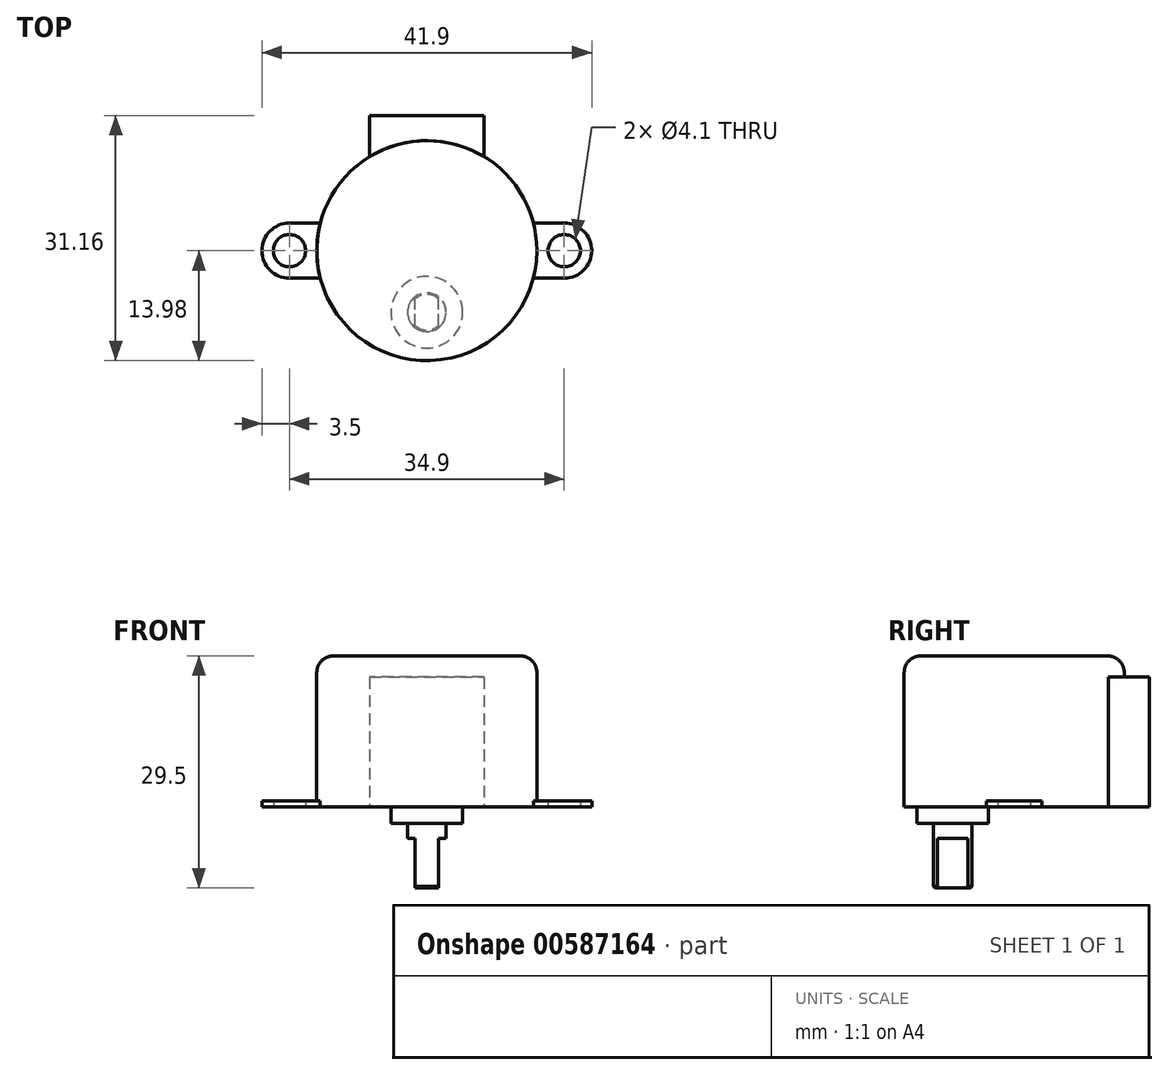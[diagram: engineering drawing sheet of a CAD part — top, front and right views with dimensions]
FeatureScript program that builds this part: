
annotation { "Feature Type Name" : "Feature", "Feature Type Description" : "" }
export const myFeature = defineFeature(function(context is Context, id is Id, definition is map)
    precondition{}
    {
        {
            var Q0;
            Q0=qCreatedBy(makeId("Top.planeOp"),FACE);
            var sketch = newSketch(context, id + "F0", { "sketchPlane" : qUnion([Q0])});
            skArc(sketch, "E0", {"start": v(13.53, 3.5) * mm, "mid": v(0, 13.97) * mm, "end": v(-13.53, 3.5) * mm});
            skLineSegment(sketch, "E1", {"start": v(0, 41.3) * mm, "end": v(0, -21.58) * mm, "construction": true});
            skLineSegment(sketch, "E2", {"start": v(0, 0) * mm, "end": v(20.95, 0) * mm, "construction": true});
            skLineSegment(sketch, "E3.0", {"start": v(13.53, -3.5) * mm, "end": v(17.45, -3.5) * mm});
            skLineSegment(sketch, "E4.0", {"start": v(13.53, 3.5) * mm, "end": v(17.45, 3.5) * mm});
            skCircle(sketch, "E5", {"center": v(17.45, 0) * mm, "radius": 2.05 * mm});
            skArc(sketch, "E6", {"start": v(17.45, -3.5) * mm, "mid": v(20.95, 0) * mm, "end": v(17.45, 3.5) * mm});
            skLineSegment(sketch, "E7.MirrorCS", {"start": v(-13.53, -3.5) * mm, "end": v(-17.45, -3.5) * mm});
            skLineSegment(sketch, "E8.MirrorCS", {"start": v(-13.53, 3.5) * mm, "end": v(-17.45, 3.5) * mm});
            skCircle(sketch, "E9.MirrorC", {"center": v(-17.45, 0) * mm, "radius": 2.05 * mm});
            skArc(sketch, "E10.MirrorCS", {"start": v(-17.45, -3.5) * mm, "mid": v(-20.95, 0) * mm, "end": v(-17.45, 3.5) * mm});
            skArc(sketch, "E11.trimOffspring", {"start": v(-13.53, -3.5) * mm, "mid": v(0, -13.97) * mm, "end": v(13.53, -3.5) * mm});
            skArc(sketch, "E12", {"start": v(-13.53, 3.5) * mm, "mid": v(-13.98, 0) * mm, "end": v(-13.53, -3.5) * mm});
            skArc(sketch, "E13.trimOffspring", {"start": v(13.53, -3.5) * mm, "mid": v(13.98, 0) * mm, "end": v(13.53, 3.5) * mm});
            skSolve(sketch);
        }
        {
            var Q0;
            Q0=makeQuery(id+"F0.imprint","IMPRINT",FACE,{"disambiguationData":[TD([[makeQuery(id+"F0.imprint","IMPRINT",EDGE,{"derivedFrom":sQuery(id+"F0.wireOp",EDGE,"E7.MirrorCS")}),-1.0]])]});
            var Q1;
            Q1=makeQuery(id+"F0.imprint","IMPRINT",FACE,{"disambiguationData":[TD([[makeQuery(id+"F0.imprint","IMPRINT",EDGE,{"derivedFrom":sQuery(id+"F0.wireOp",EDGE,"E3.0")}),1.0]])]});
            extrude(context, id + "F1", {"entities" : qUnion([Q0, Q1]), "depth" : 0.8 * mm});
        }
        {
            var Q0;
            Q0=makeQuery(id+"F0.imprint","IMPRINT",FACE,{"disambiguationData":[TD([[makeQuery(id+"F0.imprint","IMPRINT",EDGE,{"derivedFrom":sQuery(id+"F0.wireOp",EDGE,"E0")}),1.0]])]});
            extrude(context, id + "F2", {"entities" : qUnion([Q0]), "operationType" : NewBodyOperationType.ADD, "depth" : 19.2 * mm});
        }
        {
            var Q0;
            Q0=qCreatedBy(makeId("Top.planeOp"),FACE);
            var sketch = newSketch(context, id + "F3", { "sketchPlane" : qUnion([Q0])});
            skCircle(sketch, "E14", {"center": v(0, -7.82) * mm, "radius": 4.55 * mm});
            skCircle(sketch, "E15", {"center": v(0, -7.82) * mm, "radius": 2.45 * mm});
            skPoint(sketch, "E16", {"position": v(0, -3.27) * mm});
            skLineSegment(sketch, "E17.left", {"start": v(1.47, -9.78) * mm, "end": v(1.47, -5.87) * mm});
            skLineSegment(sketch, "E17.right", {"start": v(-1.48, -9.78) * mm, "end": v(-1.48, -5.87) * mm});
            skLineSegment(sketch, "E18", {"start": v(-1.48, -9.78) * mm, "end": v(1.47, -9.78) * mm, "construction": true});
            skLineSegment(sketch, "E19", {"start": v(-1.48, -5.87) * mm, "end": v(1.47, -5.87) * mm, "construction": true});
            skSolve(sketch);
        }
        {
            var Q0;
            Q0=makeQuery(id+"F3.imprint","IMPRINT",FACE,{"disambiguationData":[TD([[makeQuery(id+"F3.imprint","IMPRINT",EDGE,{"derivedFrom":sQuery(id+"F3.wireOp",EDGE,"E14")}),1.0]])]});
            extrude(context, id + "F4", {"entities" : qUnion([Q0]), "operationType" : NewBodyOperationType.ADD, "oppositeDirection" : true, "depth" : 2.1 * mm});
        }
        {
            var Q0;
            {var subQ0=sQuery(id+"F3.wireOp",EDGE,"E17.left");Q0=makeQuery(id+"F3.imprint","IMPRINT",FACE,{"disambiguationData":[TD([[makeQuery(id+"F3.imprint","IMPRINT",EDGE,{"derivedFrom":subQ0}),-1.0]])]});}
            var Q1;
            {var subQ0=sQuery(id+"F3.wireOp",EDGE,"E17.left");Q1=makeQuery(id+"F3.imprint","IMPRINT",FACE,{"disambiguationData":[TD([[makeQuery(id+"F3.imprint","IMPRINT",EDGE,{"derivedFrom":subQ0}),1.0]])]});}
            var Q2;
            {var subQ0=sQuery(id+"F3.wireOp",EDGE,"E17.right");Q2=makeQuery(id+"F3.imprint","IMPRINT",FACE,{"disambiguationData":[TD([[makeQuery(id+"F3.imprint","IMPRINT",EDGE,{"derivedFrom":subQ0}),1.0]])]});}
            extrude(context, id + "F5", {"entities" : qUnion([Q0, Q1, Q2]), "operationType" : NewBodyOperationType.ADD, "oppositeDirection" : true, "depth" : 4 * mm});
        }
        {
            var Q0;
            {var subQ0=sQuery(id+"F3.wireOp",EDGE,"E17.left");Q0=makeQuery(id+"F3.imprint","IMPRINT",FACE,{"disambiguationData":[TD([[makeQuery(id+"F3.imprint","IMPRINT",EDGE,{"derivedFrom":subQ0}),1.0]])]});}
            extrude(context, id + "F6", {"entities" : qUnion([Q0]), "operationType" : NewBodyOperationType.ADD, "oppositeDirection" : true, "depth" : 10.3 * mm});
        }
        {
            var Q0;
            Q0=qCreatedBy(makeId("Front.planeOp"),FACE);
            cPlane(context, id + "F7", {"entities" : qUnion([Q0]), "cplaneType" : CPlaneType.OFFSET, "offset" : (31.15 - 27.95 / 2) * mm, "oppositeDirection" : true, "width" : 150 * mm, "height" : 150 * mm});
        }
        {
            var Q0;
            Q0=qCreatedBy(id+"F7.planeOp",FACE);
            var sketch = newSketch(context, id + "F8", { "sketchPlane" : qUnion([Q0])});
            skLineSegment(sketch, "E20.0", {"start": v(13.53, 0) * mm, "end": v(-13.53, 0) * mm});
            skLineSegment(sketch, "E21.bottom", {"start": v(7.25, 0) * mm, "end": v(-7.25, 0) * mm});
            skLineSegment(sketch, "E21.top", {"start": v(7.25, 16.5) * mm, "end": v(-7.25, 16.5) * mm});
            skLineSegment(sketch, "E21.left", {"start": v(7.25, 0) * mm, "end": v(7.25, 16.5) * mm});
            skLineSegment(sketch, "E21.right", {"start": v(-7.25, 0) * mm, "end": v(-7.25, 16.5) * mm});
            skPoint(sketch, "E22", {"position": v(0, 0) * mm});
            skSolve(sketch);
        }
        {
            var Q0;
            Q0=qSketchRegion(id+"F8",true);
            var Q1;
            Q1=makeQuery(id+"F2.opExtrude","SWEPT_FACE",FACE,{"disambiguationData":[OSD([sQuery(id+"F0.wireOp",EDGE,"E0"),sQuery(id+"F0.wireOp",EDGE,"E11.trimOffspring"),sQuery(id+"F0.wireOp",EDGE,"E12"),sQuery(id+"F0.wireOp",EDGE,"E13.trimOffspring")])]});
            extrude(context, id + "F9", {"entities" : qUnion([Q0]), "operationType" : NewBodyOperationType.ADD, "endBound" : BoundingType.UP_TO_SURFACE, "endBoundEntityFace" : qUnion([Q1]), "depth" : 25 * mm});
        }
        {
            var Q0;
            Q0=makeQuery(id+"F2.opExtrude","CAP_FACE",FACE,{"disambiguationData":[OSD([sQuery(id+"F0.wireOp",EDGE,"E0"),sQuery(id+"F0.wireOp",EDGE,"E11.trimOffspring"),sQuery(id+"F0.wireOp",EDGE,"E12"),sQuery(id+"F0.wireOp",EDGE,"E13.trimOffspring")])],"isStart":false});
            cPlane(context, id + "F10", {"entities" : qUnion([Q0]), "cplaneType" : CPlaneType.OFFSET, "offset" : 2.05 * mm, "oppositeDirection" : true, "width" : 150 * mm, "height" : 150 * mm});
        }
        {
            var Q0;
            Q0=qCreatedBy(id+"F10.planeOp",FACE);
            var sketch = newSketch(context, id + "F11", { "sketchPlane" : qUnion([Q0])});
            skArc(sketch, "E23", {"start": v(8.62, 11.5) * mm, "mid": v(5.25, 13.38) * mm, "end": v(1.5, 14.3) * mm});
            skCircle(sketch, "E24.0", {"center": v(0, 0) * mm, "radius": 13.97 * mm});
            skLineSegment(sketch, "E25", {"start": v(8.62, 11) * mm, "end": v(8.62, 11.5) * mm});
            skLineSegment(sketch, "E26", {"start": v(-8.62, 11) * mm, "end": v(-8.62, 11.5) * mm});
            skLineSegment(sketch, "E27", {"start": v(-8.62, 11) * mm, "end": v(0, 11) * mm, "construction": true});
            skLineSegment(sketch, "E28", {"start": v(0, 11) * mm, "end": v(8.62, 11) * mm, "construction": true});
            skLineSegment(sketch, "E29", {"start": v(-8.62, 11.5) * mm, "end": v(-8.62, 13) * mm});
            skLineSegment(sketch, "E30.0", {"start": v(-7.25, 12.41) * mm, "end": v(-7.25, 13.82) * mm});
            skArc(sketch, "E31", {"start": v(-7.25, 13.82) * mm, "mid": v(-7.95, 13.43) * mm, "end": v(-8.62, 13) * mm});
            skLineSegment(sketch, "E32.MirrorCS", {"start": v(8.62, 11.5) * mm, "end": v(8.62, 13) * mm});
            skArc(sketch, "E33.MirrorCS", {"start": v(7.25, 13.82) * mm, "mid": v(7.95, 13.43) * mm, "end": v(8.62, 13) * mm});
            skLineSegment(sketch, "E34", {"start": v(7.25, 13.82) * mm, "end": v(7.25, 12.41) * mm});
            skPoint(sketch, "E35.orphan", {"position": v(-7.25, 11.95) * mm});
            skLineSegment(sketch, "E36", {"start": v(-1.5, 13.9) * mm, "end": v(-1.5, 14.3) * mm});
            skLineSegment(sketch, "E37", {"start": v(1.5, 13.9) * mm, "end": v(1.5, 14.3) * mm});
            skLineSegment(sketch, "E38", {"start": v(-1.5, 13.9) * mm, "end": v(1.5, 13.9) * mm, "construction": true});
            skPoint(sketch, "E39", {"position": v(0, 13.9) * mm});
            skLineSegment(sketch, "E40", {"start": v(0, 9.8) * mm, "end": v(0, 20.46) * mm, "construction": true});
            skArc(sketch, "E41.trimOffspring", {"start": v(-1.5, 14.3) * mm, "mid": v(-5.25, 13.38) * mm, "end": v(-8.62, 11.5) * mm});
            skSolve(sketch);
        }
        {
            var Q0;
            {var subQ0=sQuery(id+"F11.wireOp",EDGE,"E29");Q0=makeQuery(id+"F11.imprint","IMPRINT",FACE,{"disambiguationData":[TD([[makeQuery(id+"F11.imprint","IMPRINT",EDGE,{"derivedFrom":subQ0}),-1.0]])]});}
            var Q1;
            {var subQ0=sQuery(id+"F11.wireOp",EDGE,"E32.MirrorCS");Q1=makeQuery(id+"F11.imprint","IMPRINT",FACE,{"disambiguationData":[TD([[makeQuery(id+"F11.imprint","IMPRINT",EDGE,{"derivedFrom":subQ0}),1.0]])]});}
            var Q2;
            Q2=makeQuery(id+"F9.opExtrude","SWEPT_FACE",FACE,{"disambiguationData":[OSD([sQuery(id+"F8.wireOp",EDGE,"E21.top")])]});
            extrude(context, id + "F12", {"entities" : qUnion([Q0, Q1]), "operationType" : NewBodyOperationType.REMOVE, "endBound" : BoundingType.UP_TO_SURFACE, "oppositeDirection" : true, "endBoundEntityFace" : qUnion([Q2]), "depth" : 1.5 * mm});
        }
        {
            var Q0;
            Q0=makeQuery(id+"F2.opExtrude","CAP_EDGE",EDGE,{"disambiguationData":[OSD([sQuery(id+"F0.wireOp",EDGE,"E0"),sQuery(id+"F0.wireOp",EDGE,"E11.trimOffspring"),sQuery(id+"F0.wireOp",EDGE,"E12"),sQuery(id+"F0.wireOp",EDGE,"E13.trimOffspring")])],"isStart":false});
            fillet(context, id + "F13", {"entities" : qUnion([Q0]), "radius" : 2.1 * mm, "tangentPropagation" : true, "allowEdgeOverflow" : false});
        }
        {
            var Q0;
            {var subQ0=sQuery(id+"F3.wireOp",EDGE,"E15");Q0=makeQuery(id+"F6.opExtrude","CAP_EDGE",EDGE,{"disambiguationData":[OSD([subQ0]),TDD([makeQuery(id+"F3.imprint","IMPRINT",EDGE,{"disambiguationData":[TD([[makeQuery(id+"F3.imprint","INTERSECT",VERTEX,{"disambiguationData":[OD(0.0)],"derivedFrom":[subQ0,sQuery(id+"F3.wireOp",EDGE,"E17.left")]}),1.0]])],"derivedFrom":subQ0})])],"isStart":false});}
            var Q1;
            {var subQ0=sQuery(id+"F3.wireOp",EDGE,"E15");Q1=makeQuery(id+"F6.opExtrude","CAP_EDGE",EDGE,{"disambiguationData":[OSD([subQ0]),TDD([makeQuery(id+"F3.imprint","IMPRINT",EDGE,{"disambiguationData":[TD([[makeQuery(id+"F3.imprint","INTERSECT",VERTEX,{"disambiguationData":[OD(1.0)],"derivedFrom":[subQ0,sQuery(id+"F3.wireOp",EDGE,"E17.left")]}),-1.0]])],"derivedFrom":subQ0})])],"isStart":false});}
            chamfer(context, id + "F14", {"entities" : qUnion([Q0, Q1]), "width" : 0.2 * mm, "tangentPropagation" : true});
        }
    });
